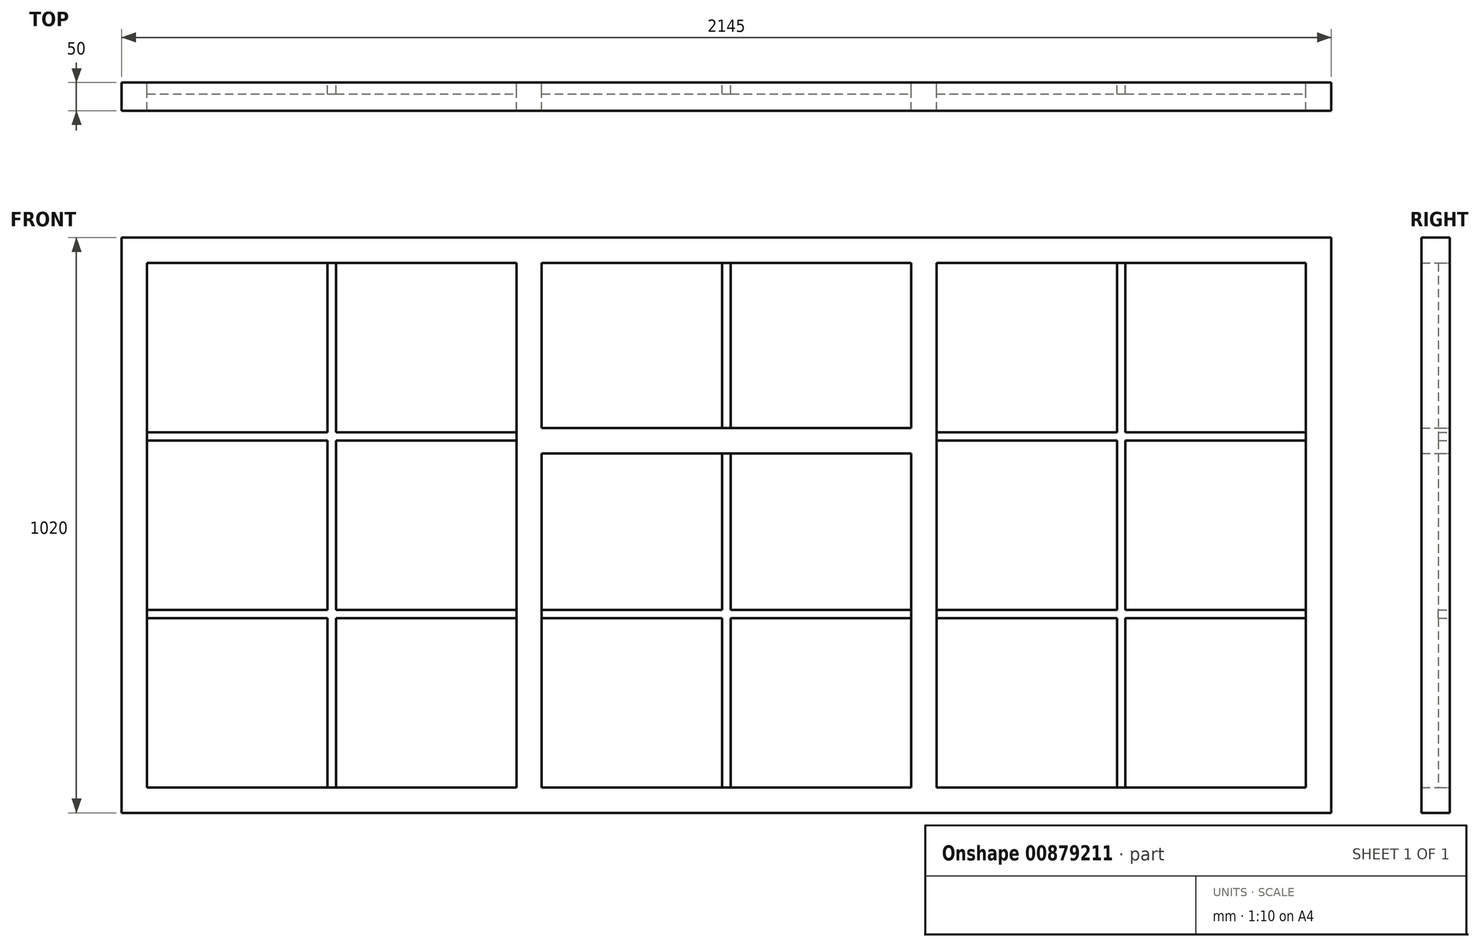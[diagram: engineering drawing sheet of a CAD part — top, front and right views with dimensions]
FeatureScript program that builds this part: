
annotation { "Feature Type Name" : "Feature", "Feature Type Description" : "" }
export const myFeature = defineFeature(function(context is Context, id is Id, definition is map)
    precondition{}
    {
        {
            var Q0;
            Q0=qCreatedBy(makeId("Front.planeOp"),FACE);
            var sketch = newSketch(context, id + "F0", { "sketchPlane" : qUnion([Q0])});
            skLineSegment(sketch, "E0.bottom", {"start": v(0, 0) * mm, "end": v(2145, 0) * mm});
            skLineSegment(sketch, "E0.top", {"start": v(0, 1020) * mm, "end": v(2145, 1020) * mm});
            skLineSegment(sketch, "E0.left", {"start": v(0, 0) * mm, "end": v(0, 1020) * mm});
            skLineSegment(sketch, "E0.right", {"start": v(2145, 0) * mm, "end": v(2145, 1020) * mm});
            skLineSegment(sketch, "E1.bottom", {"start": v(45, 975) * mm, "end": v(700, 975) * mm});
            skLineSegment(sketch, "E1.top", {"start": v(45, 45) * mm, "end": v(700, 45) * mm});
            skLineSegment(sketch, "E1.left", {"start": v(45, 975) * mm, "end": v(45, 45) * mm});
            skLineSegment(sketch, "E1.right", {"start": v(700, 975) * mm, "end": v(700, 45) * mm});
            skLineSegment(sketch, "E2.bottom", {"start": v(745, 975) * mm, "end": v(1400, 975) * mm});
            skLineSegment(sketch, "E2.top", {"start": v(745, 682.5) * mm, "end": v(1400, 682.5) * mm});
            skLineSegment(sketch, "E2.left", {"start": v(745, 975) * mm, "end": v(745, 682.5) * mm});
            skLineSegment(sketch, "E2.right", {"start": v(1400, 975) * mm, "end": v(1400, 682.5) * mm});
            skLineSegment(sketch, "E3.bottom", {"start": v(745, 637.5) * mm, "end": v(1400, 637.5) * mm});
            skLineSegment(sketch, "E3.top", {"start": v(745, 45) * mm, "end": v(1400, 45) * mm});
            skLineSegment(sketch, "E3.left", {"start": v(745, 637.5) * mm, "end": v(745, 45) * mm});
            skLineSegment(sketch, "E3.right", {"start": v(1400, 637.5) * mm, "end": v(1400, 45) * mm});
            skLineSegment(sketch, "E4.bottom", {"start": v(1445, 975) * mm, "end": v(2100, 975) * mm});
            skLineSegment(sketch, "E4.top", {"start": v(1445, 45) * mm, "end": v(2100, 45) * mm});
            skLineSegment(sketch, "E4.left", {"start": v(1445, 975) * mm, "end": v(1445, 45) * mm});
            skLineSegment(sketch, "E4.right", {"start": v(2100, 975) * mm, "end": v(2100, 45) * mm});
            skSolve(sketch);
        }
        {
            var Q0;
            Q0=qSketchRegion(id+"F0",true);
            extrude(context, id + "F1", {"entities" : qUnion([Q0]), "depth" : 50 * mm, "offsetDistance" : 25 * mm});
        }
        {
            var Q0;
            Q0=qCreatedBy(makeId("Front.planeOp"),FACE);
            var sketch = newSketch(context, id + "F2", { "sketchPlane" : qUnion([Q0])});
            skLineSegment(sketch, "E5.bottom", {"start": v(1765, 975) * mm, "end": v(1780, 975) * mm});
            skLineSegment(sketch, "E5.top", {"start": v(1765, 45) * mm, "end": v(1780, 45) * mm});
            skLineSegment(sketch, "E5.left", {"start": v(1765, 975) * mm, "end": v(1765, 660) * mm});
            skLineSegment(sketch, "E5.right", {"start": v(1780, 975) * mm, "end": v(1780, 660) * mm});
            skLineSegment(sketch, "E6.bottom", {"start": v(1445, 660) * mm, "end": v(1765, 660) * mm});
            skLineSegment(sketch, "E6.top", {"start": v(1445, 675) * mm, "end": v(1765, 675) * mm});
            skLineSegment(sketch, "E6.left", {"start": v(1445, 675) * mm, "end": v(1445, 660) * mm});
            skLineSegment(sketch, "E6.right", {"start": v(2100, 675) * mm, "end": v(2100, 660) * mm});
            skLineSegment(sketch, "E7.bottom", {"start": v(1445, 345) * mm, "end": v(1765, 345) * mm});
            skLineSegment(sketch, "E7.top", {"start": v(1445, 360) * mm, "end": v(1765, 360) * mm});
            skLineSegment(sketch, "E7.left", {"start": v(1445, 345) * mm, "end": v(1445, 360) * mm});
            skLineSegment(sketch, "E7.right", {"start": v(2100, 345) * mm, "end": v(2100, 360) * mm});
            skLineSegment(sketch, "E8.trimOffspring", {"start": v(1765, 675) * mm, "end": v(1765, 360) * mm});
            skLineSegment(sketch, "E9.trimOffspring", {"start": v(1780, 660) * mm, "end": v(2100, 660) * mm});
            skLineSegment(sketch, "E10.trimOffspring", {"start": v(1780, 675) * mm, "end": v(1780, 360) * mm});
            skLineSegment(sketch, "E11.trimOffspring", {"start": v(1780, 675) * mm, "end": v(2100, 675) * mm});
            skLineSegment(sketch, "E12.trimOffspring", {"start": v(1780, 360) * mm, "end": v(2100, 360) * mm});
            skLineSegment(sketch, "E13.trimOffspring", {"start": v(1765, 345) * mm, "end": v(1765, 45) * mm});
            skLineSegment(sketch, "E14.trimOffspring", {"start": v(1780, 345) * mm, "end": v(2100, 345) * mm});
            skLineSegment(sketch, "E15.trimOffspring", {"start": v(1780, 345) * mm, "end": v(1780, 45) * mm});
            skLineSegment(sketch, "E16.bottom", {"start": v(1065, 975) * mm, "end": v(1080, 975) * mm});
            skLineSegment(sketch, "E16.top", {"start": v(1065, 682.5) * mm, "end": v(1080, 682.5) * mm});
            skLineSegment(sketch, "E16.left", {"start": v(1065, 975) * mm, "end": v(1065, 682.5) * mm});
            skLineSegment(sketch, "E16.right", {"start": v(1080, 975) * mm, "end": v(1080, 682.5) * mm});
            skLineSegment(sketch, "E17.bottom", {"start": v(1065, 637.5) * mm, "end": v(1080, 637.5) * mm});
            skLineSegment(sketch, "E17.top", {"start": v(1065, 45) * mm, "end": v(1080, 45) * mm});
            skLineSegment(sketch, "E17.left", {"start": v(1065, 637.5) * mm, "end": v(1065, 360) * mm});
            skLineSegment(sketch, "E17.right", {"start": v(1080, 637.5) * mm, "end": v(1080, 360) * mm});
            skLineSegment(sketch, "E18.bottom", {"start": v(745, 360) * mm, "end": v(1065, 360) * mm});
            skLineSegment(sketch, "E18.top", {"start": v(745, 345) * mm, "end": v(1065, 345) * mm});
            skLineSegment(sketch, "E18.left", {"start": v(745, 360) * mm, "end": v(745, 345) * mm});
            skLineSegment(sketch, "E18.right", {"start": v(1400, 360) * mm, "end": v(1400, 345) * mm});
            skLineSegment(sketch, "E19.trimOffspring", {"start": v(1080, 360) * mm, "end": v(1400, 360) * mm});
            skLineSegment(sketch, "E20.trimOffspring", {"start": v(1065, 345) * mm, "end": v(1065, 45) * mm});
            skLineSegment(sketch, "E21.trimOffspring", {"start": v(1080, 345) * mm, "end": v(1400, 345) * mm});
            skLineSegment(sketch, "E22.trimOffspring", {"start": v(1080, 345) * mm, "end": v(1080, 45) * mm});
            skLineSegment(sketch, "E23.bottom", {"start": v(365, 975) * mm, "end": v(380, 975) * mm});
            skLineSegment(sketch, "E23.top", {"start": v(365, 45) * mm, "end": v(380, 45) * mm});
            skLineSegment(sketch, "E23.left", {"start": v(365, 975) * mm, "end": v(365, 675) * mm});
            skLineSegment(sketch, "E23.right", {"start": v(380, 975) * mm, "end": v(380, 675) * mm});
            skLineSegment(sketch, "E24.bottom", {"start": v(45, 660) * mm, "end": v(365, 660) * mm});
            skLineSegment(sketch, "E24.top", {"start": v(45, 675) * mm, "end": v(365, 675) * mm});
            skLineSegment(sketch, "E24.left", {"start": v(45, 675) * mm, "end": v(45, 660) * mm});
            skLineSegment(sketch, "E24.right", {"start": v(700, 675) * mm, "end": v(700, 660) * mm});
            skLineSegment(sketch, "E25.bottom", {"start": v(45, 360) * mm, "end": v(365, 360) * mm});
            skLineSegment(sketch, "E25.top", {"start": v(45, 345) * mm, "end": v(365, 345) * mm});
            skLineSegment(sketch, "E25.left", {"start": v(45, 360) * mm, "end": v(45, 345) * mm});
            skLineSegment(sketch, "E25.right", {"start": v(700, 360) * mm, "end": v(700, 345) * mm});
            skLineSegment(sketch, "E26.trimOffspring", {"start": v(380, 675) * mm, "end": v(700, 675) * mm});
            skLineSegment(sketch, "E27.trimOffspring", {"start": v(365, 660) * mm, "end": v(365, 360) * mm});
            skLineSegment(sketch, "E28.trimOffspring", {"start": v(380, 660) * mm, "end": v(700, 660) * mm});
            skLineSegment(sketch, "E29.trimOffspring", {"start": v(380, 660) * mm, "end": v(380, 360) * mm});
            skLineSegment(sketch, "E30.trimOffspring", {"start": v(380, 360) * mm, "end": v(700, 360) * mm});
            skLineSegment(sketch, "E31.trimOffspring", {"start": v(365, 345) * mm, "end": v(365, 45) * mm});
            skLineSegment(sketch, "E32.trimOffspring", {"start": v(380, 345) * mm, "end": v(700, 345) * mm});
            skLineSegment(sketch, "E33.trimOffspring", {"start": v(380, 345) * mm, "end": v(380, 45) * mm});
            skSolve(sketch);
        }
        {
            var Q0;
            Q0=qSketchRegion(id+"F2",true);
            extrude(context, id + "F3", {"entities" : qUnion([Q0]), "operationType" : NewBodyOperationType.ADD, "depth" : 20 * mm, "offsetDistance" : 25 * mm});
        }
    });
